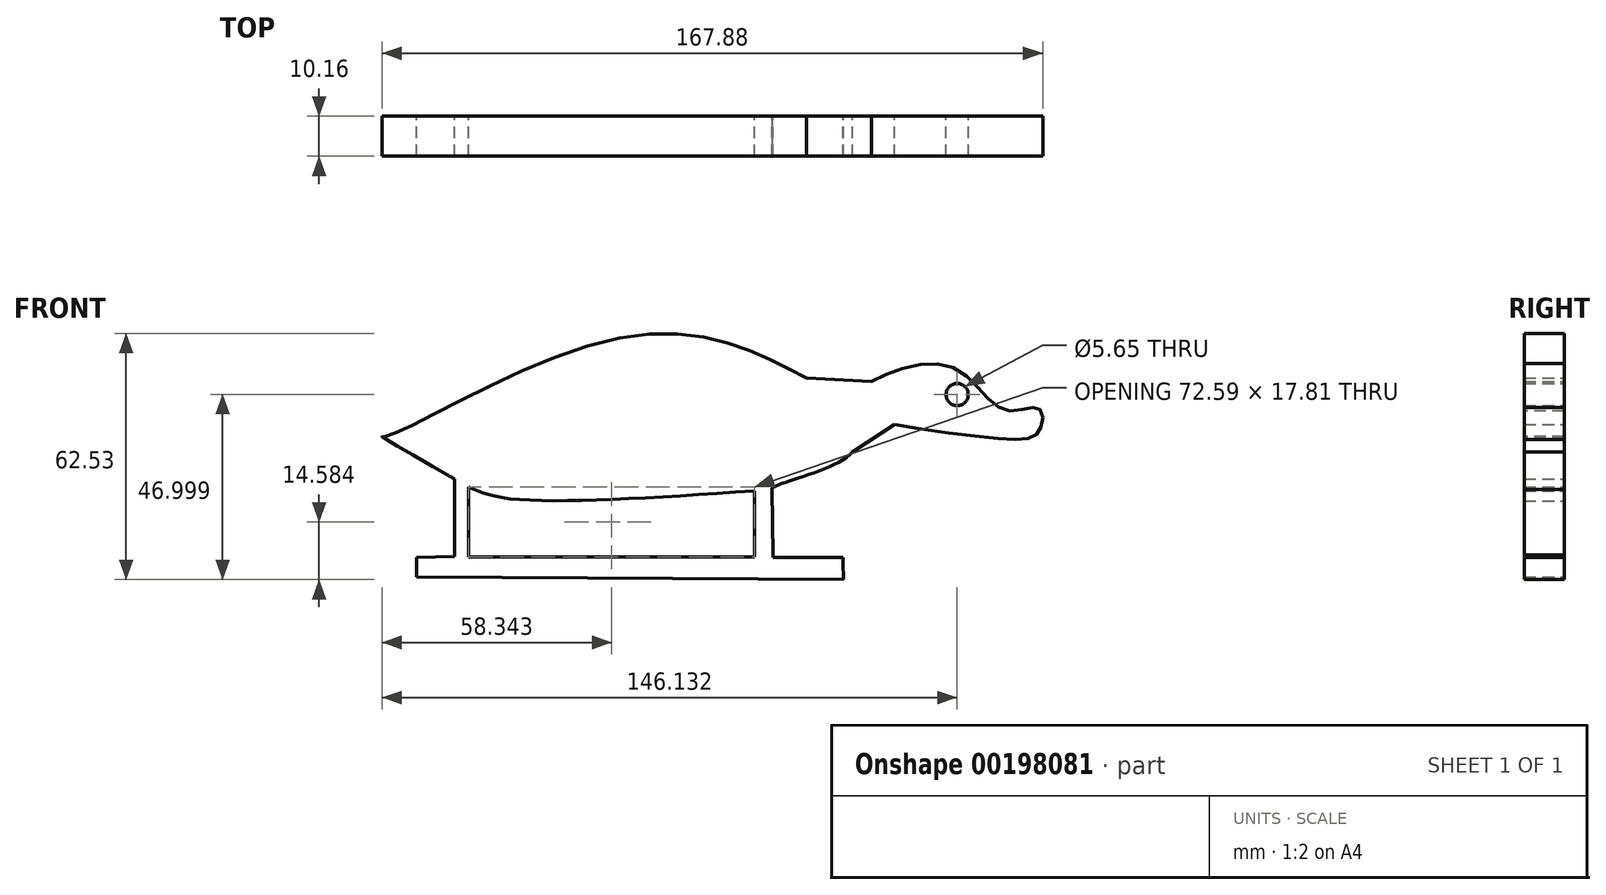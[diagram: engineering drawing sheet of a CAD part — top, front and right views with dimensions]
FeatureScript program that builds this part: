
annotation { "Feature Type Name" : "Feature", "Feature Type Description" : "" }
export const myFeature = defineFeature(function(context is Context, id is Id, definition is map)
    precondition{}
    {
        {
            var Q0;
            Q0=qCreatedBy(makeId("Front.planeOp"),FACE);
            var sketch = newSketch(context, id + "F0", { "sketchPlane" : qUnion([Q0])});
            skLineSegment(sketch, "E0", {"start": v(-43.74, -40.48) * mm, "end": v(-43.74, -57.65) * mm});
            skFitSpline(sketch, "E1", {"points": [v(-43.74, -40.48) * mm, v(-65.78, -27.7) * mm, v(-64.86, -27.66) * mm, v(-4.3, -2.34) * mm, v(41.08, -12.3) * mm, v(51.72, -18.88) * mm, v(51.74, -19.18) * mm, v(51.9, -19.17) * mm], "startDerivative": vector(-163.8, 93.74) * mm, "endDerivative": vector(12.93, 3.15) * mm});
            skFitSpline(sketch, "E2", {"points": [v(51.9, -19.17) * mm, v(58.6, -13.66) * mm, v(79.57, -10.2) * mm, v(92.4, -20.9) * mm, v(101.2, -20.6) * mm, v(101.3, -26.05) * mm, v(90.74, -28.1) * mm, v(51.9, -21) * mm, v(51.9, -19.17) * mm]});
            skFitSpline(sketch, "E3", {"points": [v(51.9, -21) * mm, v(53.7, -31.62) * mm, v(33.6, -40.53) * mm, v(33.31, -41.15) * mm], "startDerivative": vector(18.36, -30.26) * mm, "endDerivative": vector(1.05, -6.05) * mm});
            skLineSegment(sketch, "E4", {"start": v(33.31, -41.15) * mm, "end": v(33.6, -57.68) * mm});
            skLineSegment(sketch, "E5", {"start": v(41.99, -57.53) * mm, "end": v(42.42, -57.53) * mm});
            skFitSpline(sketch, "E6", {"points": [v(-43.74, -40.48) * mm, v(-33.78, -43.38) * mm, v(33.31, -41.15) * mm], "startDerivative": vector(27.1, -12.16) * mm, "endDerivative": vector(114.34, 7.9) * mm});
            skCircle(sketch, "E7", {"center": v(80.34, -16.97) * mm, "radius": 2.83 * mm});
            skLineSegment(sketch, "E8", {"start": v(42.05, -12.82) * mm, "end": v(58.6, -13.66) * mm});
            skLineSegment(sketch, "E9", {"start": v(53.7, -31.62) * mm, "end": v(64.44, -24.57) * mm});
            skLineSegment(sketch, "E10", {"start": v(-47.38, -38.4) * mm, "end": v(-47.38, -58.17) * mm});
            skLineSegment(sketch, "E11", {"start": v(28.85, -41.46) * mm, "end": v(28.85, -57.65) * mm});
            skPoint(sketch, "E12.orphan", {"position": v(33.45, -49.41) * mm});
            skPoint(sketch, "E13.end.orphan", {"position": v(42.42, -47.24) * mm});
            skPoint(sketch, "E14.end.orphan", {"position": v(37.94, -48.33) * mm});
            skPoint(sketch, "E15.orphan", {"position": v(42.42, -50.7) * mm});
            skPoint(sketch, "E16.start.orphan", {"position": v(-43.74, -55.18) * mm});
            skPoint(sketch, "E17.end.orphan", {"position": v(-33.78, -52.18) * mm});
            skLineSegment(sketch, "E18", {"start": v(33.54, -54.79) * mm, "end": v(33.45, -54.8) * mm});
            skPoint(sketch, "E19.start.orphan", {"position": v(42.42, -44.2) * mm});
            skLineSegment(sketch, "E20", {"start": v(-47.38, -58.17) * mm, "end": v(-57, -58.33) * mm});
            skLineSegment(sketch, "E21", {"start": v(-47.38, -58.17) * mm, "end": v(51.35, -58.33) * mm});
            skLineSegment(sketch, "E22", {"start": v(51.35, -58.83) * mm, "end": v(51.43, -63.97) * mm});
            skLineSegment(sketch, "E23", {"start": v(51.43, -63.97) * mm, "end": v(-57, -63.37) * mm});
            skLineSegment(sketch, "E24", {"start": v(-57, -63.37) * mm, "end": v(-57, -58.33) * mm});
            skLineSegment(sketch, "E25", {"start": v(42.42, -57.53) * mm, "end": v(42.43, -58.32) * mm});
            skLineSegment(sketch, "E26", {"start": v(41.99, -57.68) * mm, "end": v(42, -58.32) * mm});
            skLineSegment(sketch, "E27", {"start": v(41.99, -57.53) * mm, "end": v(41.99, -57.68) * mm});
            skLineSegment(sketch, "E28", {"start": v(34.1, -58.3) * mm, "end": v(34.1, -58.32) * mm});
            skLineSegment(sketch, "E29", {"start": v(37.74, -57.6) * mm, "end": v(37.75, -58.3) * mm});
            skPoint(sketch, "E30.start.orphan", {"position": v(-43.74, -52.18) * mm});
            skPoint(sketch, "E31.start.orphan", {"position": v(-33.78, -49.18) * mm});
            skPoint(sketch, "E32.end.orphan", {"position": v(-33.78, -57.65) * mm});
            skPoint(sketch, "E33.end.orphan", {"position": v(-34.57, -55.18) * mm});
            skLineSegment(sketch, "E34", {"start": v(51.35, -58.33) * mm, "end": v(51.36, -59.66) * mm});
            skPoint(sketch, "E35.start.orphan", {"position": v(31.22, -57.66) * mm});
            skPoint(sketch, "E36.end.orphan", {"position": v(37.29, -58.3) * mm});
            skLineSegment(sketch, "E37", {"start": v(28.85, -57.65) * mm, "end": v(28.85, -58.3) * mm});
            skLineSegment(sketch, "E38", {"start": v(33.6, -57.68) * mm, "end": v(33.6, -58.3) * mm});
            skLineSegment(sketch, "E39", {"start": v(-43.74, -57.65) * mm, "end": v(-43.74, -58.17) * mm});
            skSolve(sketch);
        }
        {
            var Q0;
            {var subQ1=sQuery(id+"F0.wireOp",EDGE,"E1");var subQ8=makeQuery(id+"F0.imprint","INTERSECT",VERTEX,{"derivedFrom":[subQ1,sQuery(id+"F0.wireOp",EDGE,"E8")]});Q0=makeQuery(id+"F0.imprint","IMPRINT",FACE,{"disambiguationData":[TD([[makeQuery(id+"F0.imprint","IMPRINT",EDGE,{"disambiguationData":[TD([[subQ8,1.0]])],"derivedFrom":subQ1}),-1.0]])]});}
            var Q1;
            {var subQ4=sQuery(id+"F0.wireOp",EDGE,"E0");Q1=makeQuery(id+"F0.imprint","IMPRINT",FACE,{"disambiguationData":[TD([[makeQuery(id+"F0.imprint","IMPRINT",EDGE,{"derivedFrom":subQ4}),-1.0]])]});}
            var Q2;
            {var subQ7=sQuery(id+"F0.wireOp",EDGE,"E20");Q2=makeQuery(id+"F0.imprint","IMPRINT",FACE,{"disambiguationData":[TD([[makeQuery(id+"F0.imprint","IMPRINT",EDGE,{"derivedFrom":subQ7}),1.0]])]});}
            var Q3;
            {var subQ0=sQuery(id+"F0.wireOp",EDGE,"E11");Q3=makeQuery(id+"F0.imprint","IMPRINT",FACE,{"disambiguationData":[TD([[makeQuery(id+"F0.imprint","IMPRINT",EDGE,{"derivedFrom":subQ0}),1.0]])]});}
            var Q4;
            Q4=makeQuery(id+"F0.imprint","IMPRINT",FACE,{"disambiguationData":[TD([[makeQuery(id+"F0.imprint","IMPRINT",EDGE,{"derivedFrom":sQuery(id+"F0.wireOp",EDGE,"E7")}),-1.0]])]});
            var Q5;
            {var subQ3=sQuery(id+"F0.wireOp",EDGE,"E9");Q5=makeQuery(id+"F0.imprint","IMPRINT",FACE,{"disambiguationData":[TD([[makeQuery(id+"F0.imprint","IMPRINT",EDGE,{"derivedFrom":subQ3}),1.0]])]});}
            var Q6;
            {var subQ3=sQuery(id+"F0.wireOp",EDGE,"E8");Q6=makeQuery(id+"F0.imprint","IMPRINT",FACE,{"disambiguationData":[TD([[makeQuery(id+"F0.imprint","IMPRINT",EDGE,{"derivedFrom":subQ3}),-1.0]])]});}
            extrude(context, id + "F1", {"entities" : qUnion([Q0, Q1, Q2, Q3, Q4, Q5, Q6]), "depth" : 10.16 * mm});
        }
    });
